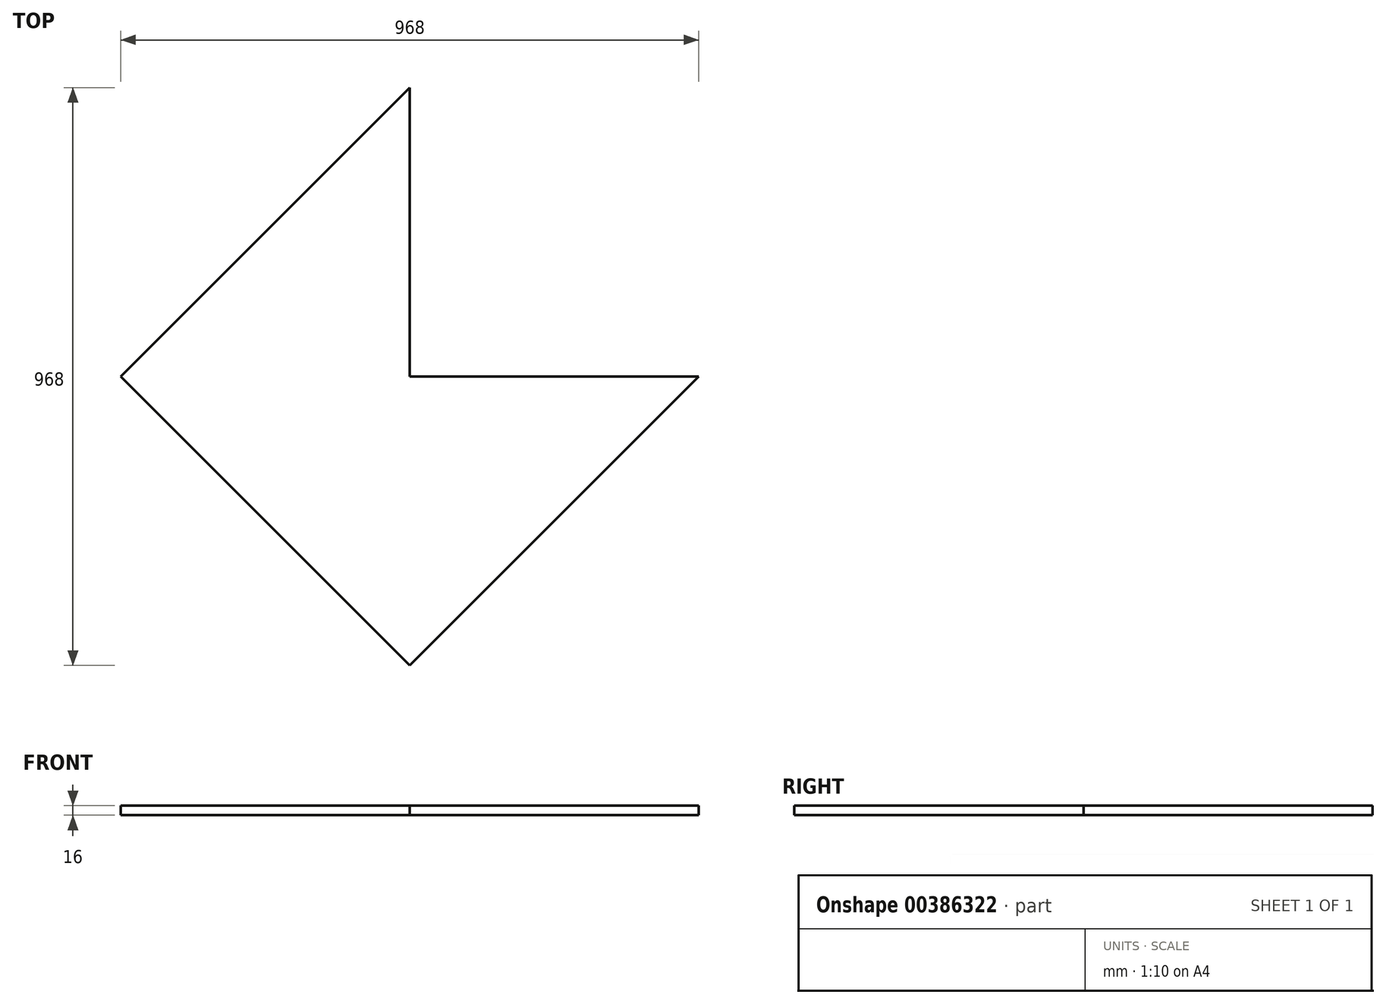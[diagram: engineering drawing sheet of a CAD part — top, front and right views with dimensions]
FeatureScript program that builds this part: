
annotation { "Feature Type Name" : "Feature", "Feature Type Description" : "" }
export const myFeature = defineFeature(function(context is Context, id is Id, definition is map)
    precondition{}
    {
        {
            var Q0;
            Q0=qCreatedBy(makeId("Top.planeOp"),FACE);
            var sketch = newSketch(context, id + "F0", { "sketchPlane" : qUnion([Q0])});
            skCircle(sketch, "E0", {"center": v(-41.67, 0) * mm, "radius": 500 * mm});
            skCircle(sketch, "E1", {"center": v(-41.67, 0) * mm, "radius": 484 * mm});
            skCircle(sketch, "E2.cCircle", {"center": v(-41.67, 0) * mm, "radius": 484 * mm, "construction": true});
            skLineSegment(sketch, "E2.0", {"start": v(-41.67, 484) * mm, "end": v(442.33, 0) * mm});
            skLineSegment(sketch, "E2.1", {"start": v(442.33, 0) * mm, "end": v(-41.67, -484) * mm});
            skLineSegment(sketch, "E2.2", {"start": v(-41.67, -484) * mm, "end": v(-525.67, 0) * mm});
            skLineSegment(sketch, "E2.3", {"start": v(-525.67, 0) * mm, "end": v(-41.67, 484) * mm});
            skLineSegment(sketch, "E3", {"start": v(-41.67, 484) * mm, "end": v(-41.67, -484) * mm});
            skLineSegment(sketch, "E4", {"start": v(-525.67, 0) * mm, "end": v(442.33, 0) * mm});
            skLineSegment(sketch, "E5", {"start": v(-525.67, 0) * mm, "end": v(-541.67, 0) * mm});
            skLineSegment(sketch, "E6", {"start": v(-41.67, 484) * mm, "end": v(-41.67, 500) * mm});
            skLineSegment(sketch, "E7", {"start": v(-41.67, -484) * mm, "end": v(-41.67, -500) * mm});
            skLineSegment(sketch, "E8", {"start": v(442.33, 0) * mm, "end": v(458.33, 0) * mm});
            skLineSegment(sketch, "E9.2", {"start": v(442.33, 0) * mm, "end": v(-41.67, 484) * mm});
            skLineSegment(sketch, "E10.bottom", {"start": v(-525.67, 0) * mm, "end": v(-41.67, 0) * mm});
            skLineSegment(sketch, "E10.right", {"start": v(-41.67, 0) * mm, "end": v(-41.67, 484) * mm});
            skLineSegment(sketch, "E11.right", {"start": v(-41.67, 0) * mm, "end": v(-41.67, -484) * mm});
            skLineSegment(sketch, "E12.bottom", {"start": v(-41.67, 0) * mm, "end": v(458.33, 0) * mm});
            skLineSegment(sketch, "E12.top", {"start": v(-41.67, 0) * mm, "end": v(458.33, 0) * mm});
            skLineSegment(sketch, "E12.left", {"start": v(-41.67, 0) * mm, "end": v(-41.67, 0) * mm});
            skLineSegment(sketch, "E12.right", {"start": v(458.33, 0) * mm, "end": v(458.33, 0) * mm});
            skLineSegment(sketch, "E13.top", {"start": v(-41.67, 0) * mm, "end": v(442.33, 0) * mm});
            skLineSegment(sketch, "E13.left", {"start": v(-41.67, -484) * mm, "end": v(-41.67, 0) * mm});
            skSolve(sketch);
        }
        {
            var Q0;
            Q0=makeQuery(id+"F0.imprint","IMPRINT",FACE,{"disambiguationData":[TD([[makeQuery(id+"F0.imprint","IMPRINT",EDGE,{"derivedFrom":sQuery(id+"F0.wireOp",EDGE,"E9.2")}),1.0]])]});
            var Q1;
            Q1=makeQuery(id+"F0.imprint","IMPRINT",FACE,{"disambiguationData":[TD([[makeQuery(id+"F0.imprint","IMPRINT",EDGE,{"derivedFrom":sQuery(id+"F0.wireOp",EDGE,"E2.3")}),-1.0]])]});
            var Q2;
            Q2=makeQuery(id+"F0.imprint","IMPRINT",FACE,{"disambiguationData":[TD([[makeQuery(id+"F0.imprint","IMPRINT",EDGE,{"derivedFrom":sQuery(id+"F0.wireOp",EDGE,"E2.2")}),-1.0]])]});
            var Q3;
            Q3=makeQuery(id+"F0.imprint","IMPRINT",FACE,{"disambiguationData":[TD([[makeQuery(id+"F0.imprint","IMPRINT",EDGE,{"derivedFrom":sQuery(id+"F0.wireOp",EDGE,"E2.1")}),-1.0]])]});
            extrude(context, id + "F1", {"entities" : qUnion([Q0, Q1, Q2, Q3]), "depth" : 16 * mm});
        }
    });
